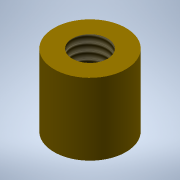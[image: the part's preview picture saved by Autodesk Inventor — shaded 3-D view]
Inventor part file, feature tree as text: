
AUTODESK INVENTOR PART (.ipt)
format: ipt  version: 2022.6 (Build 266554000, 554)  size: 97,280 bytes
history: native  units: mm
features: extrude x1, hole x1
ambient origin geometry x8: Origin, YZ Plane, XZ Plane, XY Plane, X Axis, Y Axis, Z Axis, Center Point
bodies: Solid1 (feature_tree)
feature tree (2):
  extrude  "Extrusion1"  Depth=5.0mm
  hole  "Hole1"  [1 undecoded]
note: 1 required parameter value undecoded (feature->parameter linkage not recoverable at this tier; creation-order binding heuristic only, values carry confidence <= 0.55)
